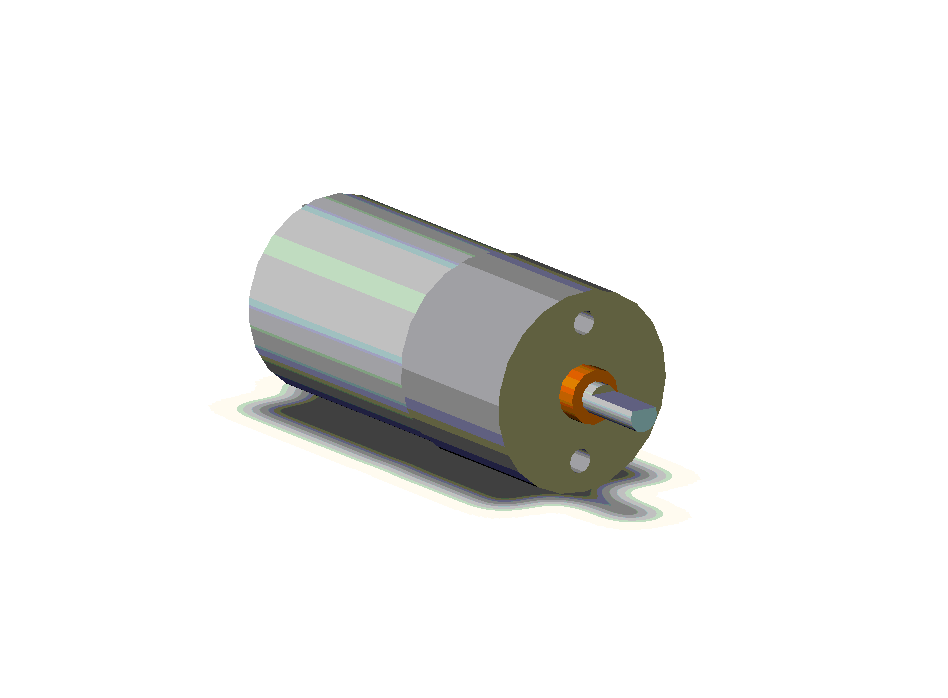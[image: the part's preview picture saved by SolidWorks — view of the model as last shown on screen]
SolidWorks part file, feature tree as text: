
SOLIDWORKS PART (.sldprt)
format: sldprt  version: not decoded by parser v0  size: 379,392 bytes
history: native  units: mm
features: sketch x9, extrude x6, cut_extrude x3, fillet x2 (+8 scaffold rows collapsed)
feature tree (28):
  scaffold x8  (default folders/planes/origin — collapsed)
  sketch  "Sketch2"  dims[D1=24.8mm]
  extrude  "Base-Extrude"  Depth=19.05mm
  sketch  "Sketch3"  dims[D1=6.83mm]
  extrude  "Boss-Extrude1"  Depth=2.54mm
  sketch  "Sketch5"  dims[D1=3.88mm]
  extrude  "Boss-Extrude2"  Depth=9.55mm
  sketch  "Sketch6"  dims[D2=2.5mm D1=~0.894972mm]
  cut_extrude  "Cut-Extrude1"  Depth=8mm
  sketch  "Sketch7"  dims[D1=24.0mm]
  extrude  "Boss-Extrude3"  Depth=30.25mm
  sketch  "Sketch8"  dims[D2=8.38mm D1=3.2mm]
  extrude  "Boss-Extrude4"  Depth=2mm
  sketch  "Sketch9"  dims[D1=19.05mm D2=0.21mm D3=0.21mm D4=9.525mm D5=2.8mm D6=1.4mm D7=1.4mm D8=2.8mm]
  extrude  "Boss-Extrude5"  Depth=5mm
  fillet  "Fillet1"  Radius=1.4mm
  fillet  "Fillet2"  Radius=1.4mm
  sketch  "Sketch10"  dims[D1=0.8mm]
  cut_extrude  "Cut-Extrude2"  [1 undecoded]
  sketch  "Sketch11"  dims[D3=3.0mm D4=3.0mm D1=8.5mm D2=8.5mm]
  cut_extrude  "Cut-Extrude3"  Depth=4mm
decode coverage: 19 of 20 modeling features carry decoded parameters
note: ~ marks probable driven/reference dimensions
note: 1 parameter value undecoded
note: suppression state not decoded; provenance and decode notes live in map.json
